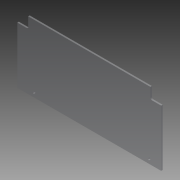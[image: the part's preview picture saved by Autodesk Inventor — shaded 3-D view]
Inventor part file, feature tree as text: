
AUTODESK INVENTOR PART (.ipt)
format: ipt  version: 2013 (Build 170138000, 138)  size: 100,864 bytes
history: native  units: in
note: dims shown in document units (in); Inventor stores cm internally (conversion verified against a paired STEP export)
features: sketch x3, extrude x2, fillet x1, plane x1, mirror x1, hole x1
ambient origin geometry x8: Origin, YZ Plane, XZ Plane, XY Plane, X Axis, Y Axis, Z Axis, Center Point
bodies: Solid1 (feature_tree)
feature tree (9):
  extrude  "Extrusion1"  Depth=10.88in
  extrude  "Extrusion2"  Depth=1.75in
  fillet  "Fillet1"  Radius=9.13in
  plane  "Work Plane1"
  mirror  "Mirror1"
  hole  "Hole1"  [1 undecoded]
  sketch  "Sketch1"  dims[d0=23.25in d1=10.88in]
  sketch  "Sketch2"  dims[d2=0.25in d3=0.0in d4=1.75in d6=9.13in]
  sketch  "Sketch3"  dims[d7=0.25in d8=0.0in d9=0.25in d10=2.63in d11=21.25in d12=0.63in d13=0.27in d14=0.75in d15=0.375in d16=0.25in d17=0.5635in d18=1.0in d19=0.8108in]
note: 1 required parameter value undecoded (feature->parameter linkage not recoverable at this tier; creation-order binding heuristic only, values carry confidence <= 0.55)
